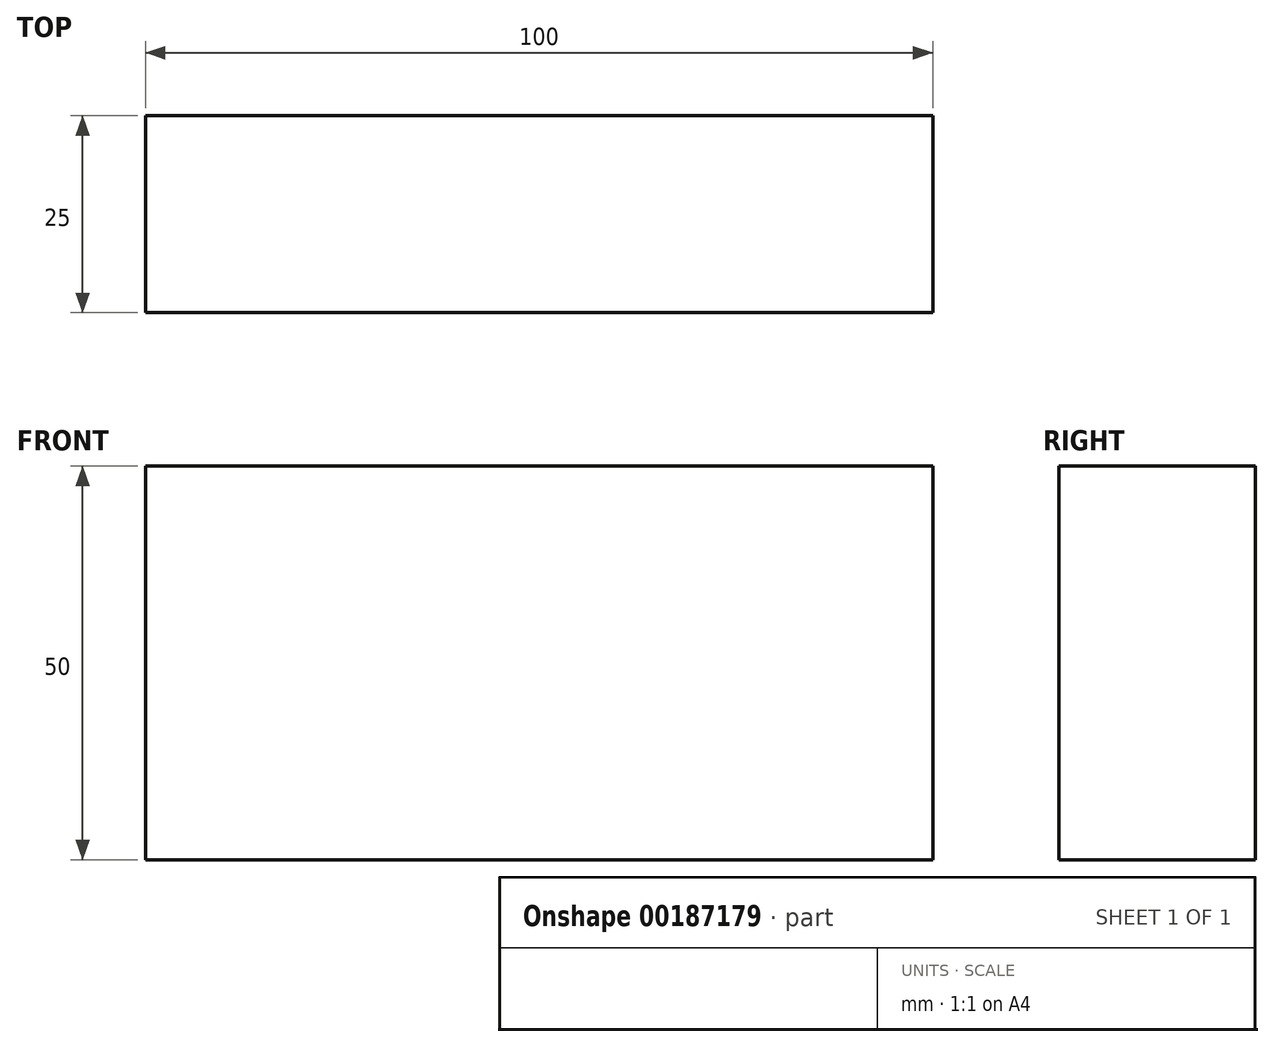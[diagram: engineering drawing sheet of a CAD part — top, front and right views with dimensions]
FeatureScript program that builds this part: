
annotation { "Feature Type Name" : "Feature", "Feature Type Description" : "" }
export const myFeature = defineFeature(function(context is Context, id is Id, definition is map)
    precondition{}
    {
        {
            var Q0;
            Q0=qCreatedBy(makeId("Front.planeOp"),FACE);
            var sketch = newSketch(context, id + "F0", { "sketchPlane" : qUnion([Q0])});
            skLineSegment(sketch, "E0.bottom", {"start": v(-48.04, 25) * mm, "end": v(51.96, 25) * mm});
            skLineSegment(sketch, "E0.top", {"start": v(-48.04, -25) * mm, "end": v(51.96, -25) * mm});
            skLineSegment(sketch, "E0.left", {"start": v(-48.04, 25) * mm, "end": v(-48.04, -25) * mm});
            skLineSegment(sketch, "E0.right", {"start": v(51.96, 25) * mm, "end": v(51.96, -25) * mm});
            skPoint(sketch, "E0.middle", {"position": v(1.96, 0) * mm});
            skSolve(sketch);
        }
        {
            var Q0;
            Q0 = qSketchRegion(id + "F0", true);
            extrude(context, id + "F1", {"entities" : qUnion([Q0]), "depth" : 25 * mm});
        }
    });
